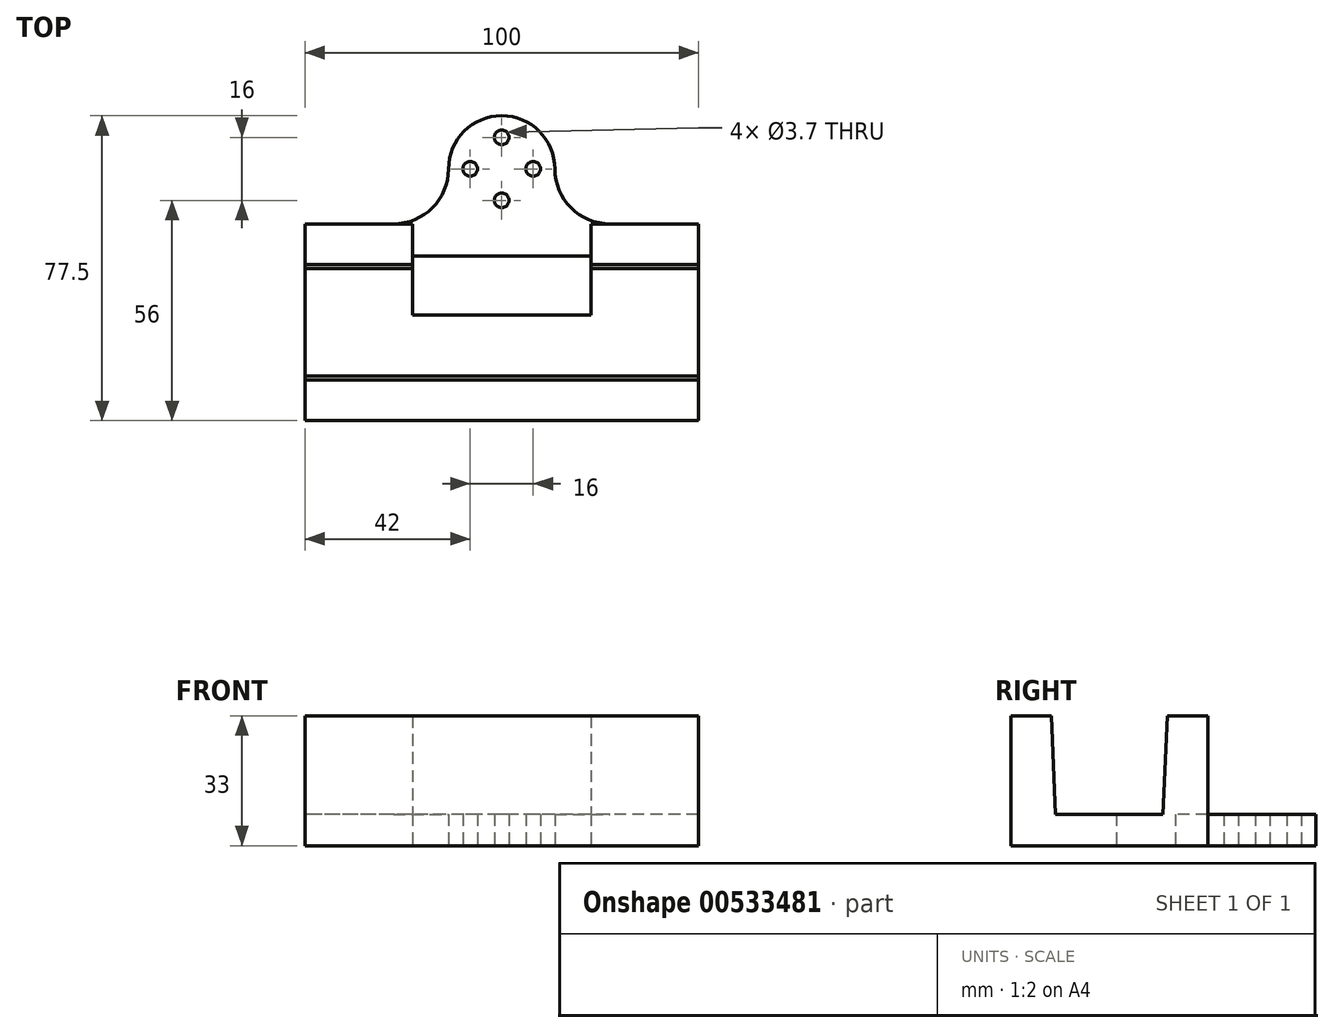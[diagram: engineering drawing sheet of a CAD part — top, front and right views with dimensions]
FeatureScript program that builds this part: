
annotation { "Feature Type Name" : "Feature", "Feature Type Description" : "" }
export const myFeature = defineFeature(function(context is Context, id is Id, definition is map)
    precondition{}
    {
        {
            var Q0;
            Q0=qCreatedBy(makeId("Top.planeOp"),FACE);
            var sketch = newSketch(context, id + "F0", { "sketchPlane" : qUnion([Q0])});
            skArc(sketch, "E0", {"start": v(13.5, 0) * mm, "mid": v(0, 13.5) * mm, "end": v(-13.5, 0) * mm});
            skCircle(sketch, "E1", {"center": v(0, 0) * mm, "radius": 8 * mm, "construction": true});
            skLineSegment(sketch, "E2", {"start": v(13.5, 0) * mm, "end": v(-13.5, 0) * mm, "construction": true});
            skLineSegment(sketch, "E3", {"start": v(0, -13.5) * mm, "end": v(0, 13.5) * mm, "construction": true});
            skCircle(sketch, "E4", {"center": v(0, 8) * mm, "radius": 1.85 * mm});
            skCircle(sketch, "E5", {"center": v(8, 0) * mm, "radius": 1.85 * mm});
            skCircle(sketch, "E6", {"center": v(0, -8) * mm, "radius": 1.85 * mm});
            skCircle(sketch, "E7", {"center": v(-8, 0) * mm, "radius": 1.85 * mm});
            skLineSegment(sketch, "E8", {"start": v(-13.5, 0) * mm, "end": v(-13.5, 0) * mm});
            skLineSegment(sketch, "E9", {"start": v(-27.5, -14) * mm, "end": v(-50, -14) * mm});
            skLineSegment(sketch, "E10", {"start": v(-50, -14) * mm, "end": v(-50, -64) * mm});
            skLineSegment(sketch, "E11", {"start": v(-50, -64) * mm, "end": v(50, -64) * mm});
            skLineSegment(sketch, "E12", {"start": v(50, -64) * mm, "end": v(50, -14) * mm});
            skLineSegment(sketch, "E13", {"start": v(50, -14) * mm, "end": v(27.5, -14) * mm});
            skLineSegment(sketch, "E14", {"start": v(13.5, 0) * mm, "end": v(13.5, 0) * mm});
            skLineSegment(sketch, "E15", {"start": v(-50, -14) * mm, "end": v(-27.5, -14) * mm, "construction": true});
            skLineSegment(sketch, "E16", {"start": v(0, -64) * mm, "end": v(0, 13.5) * mm, "construction": true});
            skArc(sketch, "E17.filletArc", {"start": v(-27.5, -14) * mm, "mid": v(-17.6, -9.9) * mm, "end": v(-13.5, 0) * mm});
            skPoint(sketch, "E18.visualSharp", {"position": v(13.5, -14) * mm});
            skArc(sketch, "E18.filletArc", {"start": v(13.5, 0) * mm, "mid": v(17.6, -9.9) * mm, "end": v(27.5, -14) * mm});
            skLineSegment(sketch, "E19", {"start": v(-50, -14) * mm, "end": v(50, -14) * mm, "construction": true});
            skLineSegment(sketch, "E20", {"start": v(50, -39) * mm, "end": v(-50, -39) * mm, "construction": true});
            skLineSegment(sketch, "E21.bottom", {"start": v(-47.13, -52.85) * mm, "end": v(47.12, -52.85) * mm, "construction": true});
            skLineSegment(sketch, "E21.top", {"start": v(-47.13, -25.15) * mm, "end": v(47.12, -25.15) * mm, "construction": true});
            skLineSegment(sketch, "E21.left", {"start": v(-47.13, -52.85) * mm, "end": v(-47.13, -25.15) * mm, "construction": true});
            skLineSegment(sketch, "E21.right", {"start": v(47.12, -52.85) * mm, "end": v(47.12, -25.15) * mm, "construction": true});
            skPoint(sketch, "E21.middle", {"position": v(0, -39) * mm});
            skLineSegment(sketch, "E22", {"start": v(22.68, -22.15) * mm, "end": v(-22.68, -22.15) * mm});
            skLineSegment(sketch, "E23", {"start": v(-22.68, -22.15) * mm, "end": v(-22.68, -37.15) * mm});
            skLineSegment(sketch, "E24", {"start": v(-22.68, -37.15) * mm, "end": v(22.68, -37.15) * mm});
            skLineSegment(sketch, "E25", {"start": v(22.68, -37.15) * mm, "end": v(22.68, -22.15) * mm});
            skSolve(sketch);
        }
        {
            var Q0;
            Q0=makeQuery(id+"F0.imprint","IMPRINT",FACE,{"disambiguationData":[TD([[makeQuery(id+"F0.imprint","IMPRINT",EDGE,{"derivedFrom":sQuery(id+"F0.wireOp",EDGE,"E0")}),1.0]])]});
            extrude(context, id + "F1", {"entities" : qUnion([Q0]), "depth" : 8 * mm, "offsetDistance" : 25 * mm});
        }
        {
            var Q0;
            Q0=makeQuery(id+"F1.opExtrude","CAP_FACE",FACE,{"disambiguationData":[OSD([sQuery(id+"F0.wireOp",EDGE,"E0"),sQuery(id+"F0.wireOp",EDGE,"E4"),sQuery(id+"F0.wireOp",EDGE,"E5"),sQuery(id+"F0.wireOp",EDGE,"E6"),sQuery(id+"F0.wireOp",EDGE,"E7"),sQuery(id+"F0.wireOp",EDGE,"E9"),sQuery(id+"F0.wireOp",EDGE,"E10"),sQuery(id+"F0.wireOp",EDGE,"E11"),sQuery(id+"F0.wireOp",EDGE,"E12"),sQuery(id+"F0.wireOp",EDGE,"E13"),sQuery(id+"F0.wireOp",EDGE,"E17.filletArc"),sQuery(id+"F0.wireOp",EDGE,"E18.filletArc"),sQuery(id+"F0.wireOp",EDGE,"E22"),sQuery(id+"F0.wireOp",EDGE,"E23"),sQuery(id+"F0.wireOp",EDGE,"E24"),sQuery(id+"F0.wireOp",EDGE,"E25")])],"isStart":false});
            var sketch = newSketch(context, id + "F2", { "sketchPlane" : qUnion([Q0])});
            skLineSegment(sketch, "E26", {"start": v(-50, -14) * mm, "end": v(-50, -64) * mm});
            skLineSegment(sketch, "E27", {"start": v(-50, -64) * mm, "end": v(50, -64) * mm});
            skLineSegment(sketch, "E28", {"start": v(50, -64) * mm, "end": v(50, -14) * mm});
            skLineSegment(sketch, "E29", {"start": v(50, -14) * mm, "end": v(-50, -14) * mm, "construction": true});
            skLineSegment(sketch, "E30", {"start": v(-22.68, -37.15) * mm, "end": v(22.68, -37.15) * mm});
            skLineSegment(sketch, "E31", {"start": v(0, 13.5) * mm, "end": v(0, -64) * mm, "construction": true});
            skLineSegment(sketch, "E32", {"start": v(-50, -14) * mm, "end": v(-22.68, -14) * mm});
            skLineSegment(sketch, "E33", {"start": v(-22.68, -14) * mm, "end": v(-22.68, -37.15) * mm});
            skLineSegment(sketch, "E34", {"start": v(50, -14) * mm, "end": v(22.68, -14) * mm});
            skLineSegment(sketch, "E35", {"start": v(22.68, -14) * mm, "end": v(22.68, -37.15) * mm});
            skSolve(sketch);
        }
        {
            var Q0;
            {var subQ12=sQuery(id+"F2.wireOp",EDGE,"E26");Q0=makeQuery(id+"F2.imprint","IMPRINT",FACE,{"disambiguationData":[TD([[makeQuery(id+"F2.imprint","IMPRINT",EDGE,{"derivedFrom":subQ12}),1.0]])]});}
            extrude(context, id + "F3", {"entities" : qUnion([Q0]), "operationType" : NewBodyOperationType.ADD, "depth" : 25 * mm, "offsetDistance" : 25 * mm});
        }
        {
            var Q0;
            Q0=makeQuery(id+"F3.boolean.opBoolean","MERGE",FACE,{"derivedFrom":[makeQuery(id+"F1.opExtrude","SWEPT_FACE",FACE,{"disambiguationData":[OSD([sQuery(id+"F0.wireOp",EDGE,"E10")])]}),makeQuery(id+"F3.opExtrude","SWEPT_FACE",FACE,{"disambiguationData":[OSD([sQuery(id+"F2.wireOp",EDGE,"E26")])]})]});
            var sketch = newSketch(context, id + "F4", { "sketchPlane" : qUnion([Q0])});
            skLineSegment(sketch, "E36", {"start": v(39, 33) * mm, "end": v(39, 0) * mm, "construction": true});
            skLineSegment(sketch, "E37", {"start": v(25.35, 8) * mm, "end": v(52.65, 8) * mm});
            skLineSegment(sketch, "E38", {"start": v(52.65, 8) * mm, "end": v(53.7, 33) * mm});
            skLineSegment(sketch, "E39", {"start": v(53.7, 33) * mm, "end": v(24.3, 33) * mm});
            skLineSegment(sketch, "E40", {"start": v(24.3, 33) * mm, "end": v(25.35, 8) * mm});
            skLineSegment(sketch, "E41", {"start": v(24.34, 32) * mm, "end": v(53.66, 32) * mm, "construction": true});
            skSolve(sketch);
        }
        {
            var Q0;
            Q0=makeQuery(id+"F4.imprint","IMPRINT",FACE,{"disambiguationData":[TD([[makeQuery(id+"F4.imprint","IMPRINT",EDGE,{"derivedFrom":sQuery(id+"F4.wireOp",EDGE,"E37")}),1.0]])]});
            var Q1;
            Q1=makeQuery(id+"F3.boolean.opBoolean","MERGE",FACE,{"derivedFrom":[makeQuery(id+"F1.opExtrude","SWEPT_FACE",FACE,{"disambiguationData":[OSD([sQuery(id+"F0.wireOp",EDGE,"E12")])]}),makeQuery(id+"F3.opExtrude","SWEPT_FACE",FACE,{"disambiguationData":[OSD([sQuery(id+"F2.wireOp",EDGE,"E28")])]})]});
            extrude(context, id + "F5", {"entities" : qUnion([Q0]), "operationType" : NewBodyOperationType.REMOVE, "endBound" : BoundingType.UP_TO_SURFACE, "oppositeDirection" : true, "depth" : 25 * mm, "endBoundEntityFace" : qUnion([Q1]), "offsetDistance" : 25 * mm});
        }
    });
